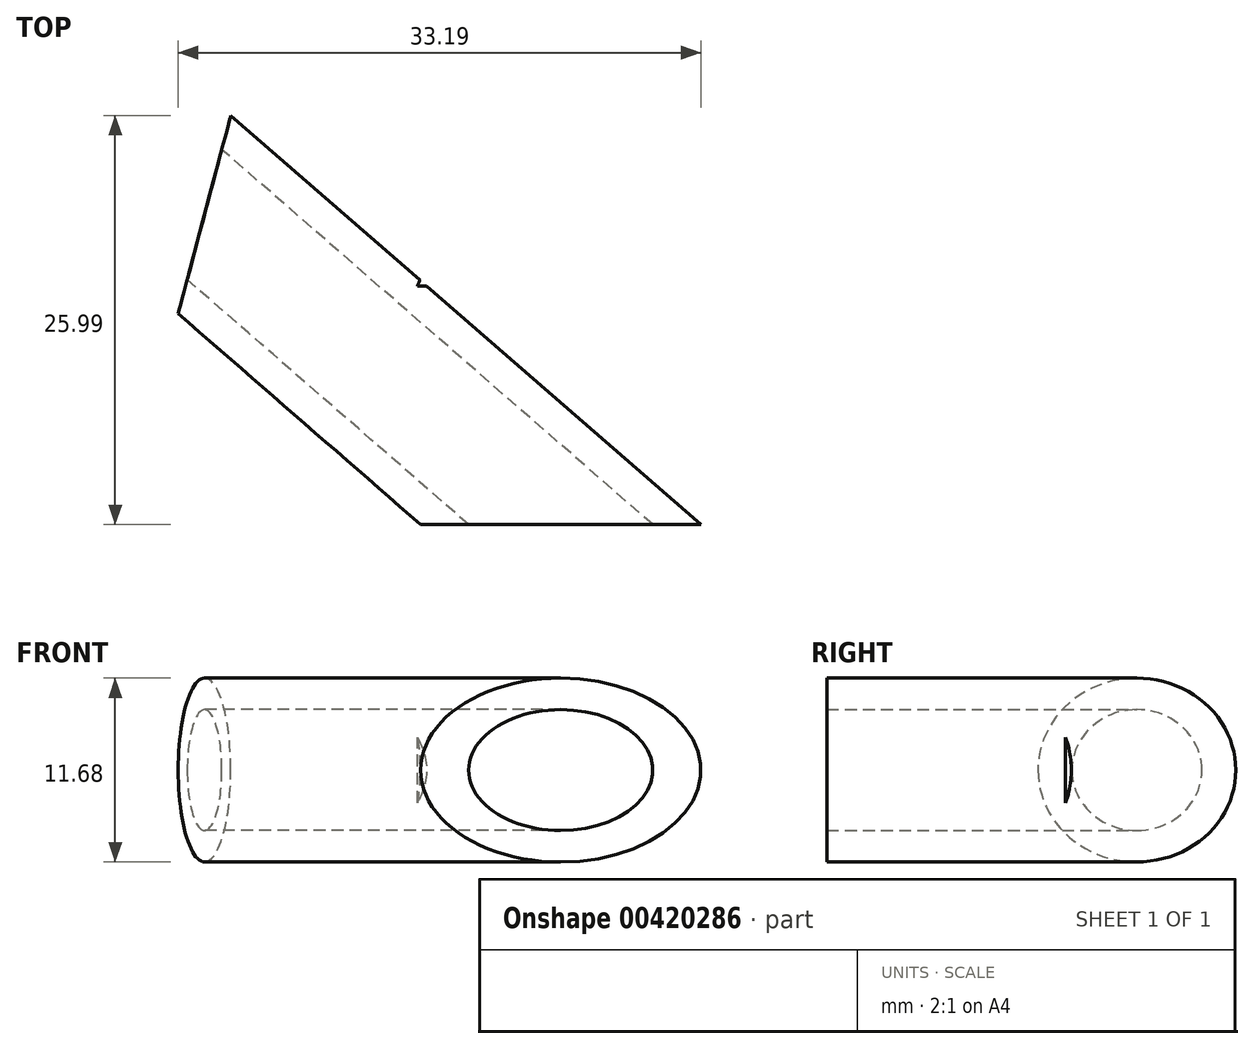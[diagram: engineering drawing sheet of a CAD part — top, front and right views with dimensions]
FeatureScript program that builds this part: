
annotation { "Feature Type Name" : "Feature", "Feature Type Description" : "" }
export const myFeature = defineFeature(function(context is Context, id is Id, definition is map)
    precondition{}
    {
        {
            var Q0;
            Q0=qCreatedBy(makeId("Top.planeOp"),FACE);
            var sketch = newSketch(context, id + "F0", { "sketchPlane" : qUnion([Q0])});
            skLineSegment(sketch, "E0", {"start": v(-29.17, 18.15) * mm, "end": v(18.61, -23.44) * mm});
            skLineSegment(sketch, "E1", {"start": v(18.61, -23.44) * mm, "end": v(22.45, -19.04) * mm});
            skLineSegment(sketch, "E2", {"start": v(22.45, -19.04) * mm, "end": v(-25.34, 22.55) * mm});
            skLineSegment(sketch, "E3", {"start": v(-25.34, 22.55) * mm, "end": v(-29.17, 18.15) * mm});
            skSolve(sketch);
        }
        {
            var Q0;
            Q0=makeQuery(id+"F0.imprint","IMPRINT",FACE,{"disambiguationData":[TD([[makeQuery(id+"F0.imprint","IMPRINT",EDGE,{"derivedFrom":sQuery(id+"F0.wireOp",EDGE,"E0")}),1.0]])]});
            var Q1;
            Q1=sQuery(id+"F0.wireOp",EDGE,"E0");
            revolve(context, id + "F1", {"entities" : qUnion([Q0]), "axis" : qUnion([Q1]), "revolveType" : RevolveType.FULL});
        }
        {
            var Q0;
            Q0=makeQuery(id+"F1.opRevolve","SWEPT_FACE",FACE,{"disambiguationData":[OSD([sQuery(id+"F0.wireOp",EDGE,"E3")])]});
            var Q1;
            Q1=makeQuery(id+"F1.opRevolve","SWEPT_FACE",FACE,{"disambiguationData":[OSD([sQuery(id+"F0.wireOp",EDGE,"E1")])]});
            shell(context, id + "F2", {"entities" : qUnion([Q0, Q1]), "thickness" : 2 * mm});
        }
        {
            var Q0;
            Q0=qCreatedBy(makeId("Top.planeOp"),FACE);
            cPlane(context, id + "F3", {"entities" : qUnion([Q0]), "cplaneType" : CPlaneType.OFFSET, "offset" : 25 * mm, "width" : 150 * mm, "height" : 150 * mm});
        }
        {
            var Q0;
            Q0=qCreatedBy(id+"F3.planeOp",FACE);
            var sketch = newSketch(context, id + "F4", { "sketchPlane" : qUnion([Q0])});
            skLineSegment(sketch, "E4", {"start": v(-10.22, -15.17) * mm, "end": v(26.5, -15.17) * mm});
            skLineSegment(sketch, "E5", {"start": v(26.5, -15.17) * mm, "end": v(26.5, 0) * mm});
            skLineSegment(sketch, "E6", {"start": v(26.5, 0) * mm, "end": v(0, 0) * mm});
            skLineSegment(sketch, "E7", {"start": v(-17.06, -8.81) * mm, "end": v(-9.57, 19.42) * mm});
            skLineSegment(sketch, "E8", {"start": v(-9.57, 19.42) * mm, "end": v(5.96, 13.98) * mm});
            skLineSegment(sketch, "E9", {"start": v(5.96, 13.98) * mm, "end": v(0, 0) * mm});
            skLineSegment(sketch, "E10", {"start": v(-10.22, -15.17) * mm, "end": v(-17.06, -8.81) * mm});
            skSolve(sketch);
        }
        {
            var Q0;
            Q0=makeQuery(id+"F4.imprint","IMPRINT",FACE,{"disambiguationData":[TD([[makeQuery(id+"F4.imprint","IMPRINT",EDGE,{"derivedFrom":sQuery(id+"F4.wireOp",EDGE,"E4")}),1.0]])]});
            extrude(context, id + "F5", {"entities" : qUnion([Q0]), "operationType" : NewBodyOperationType.INTERSECT, "oppositeDirection" : true, "depth" : 50 * mm});
        }
    });
